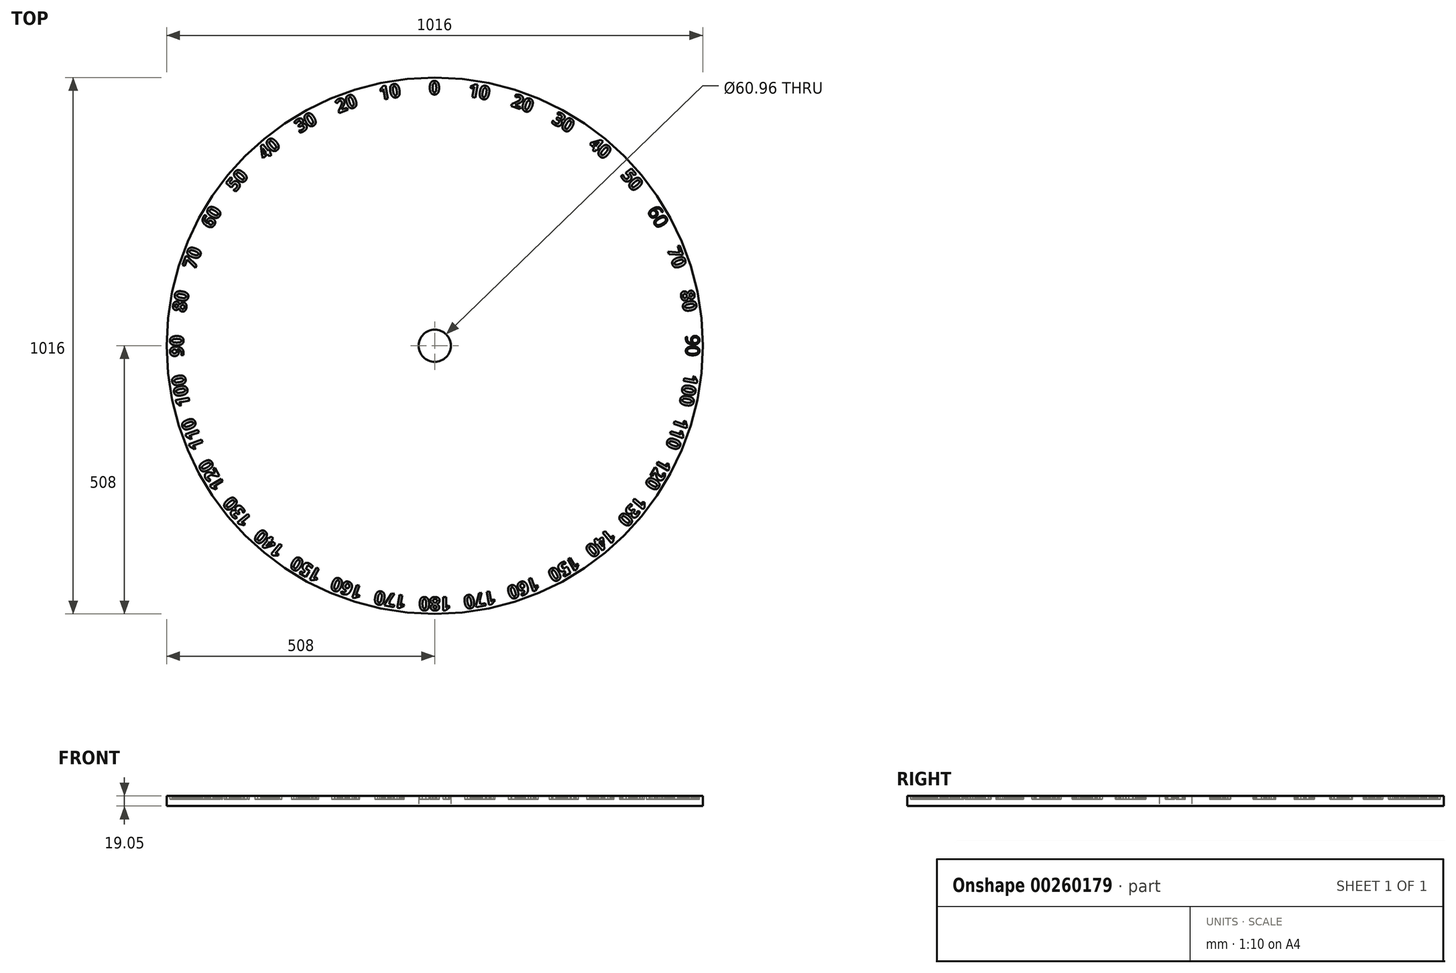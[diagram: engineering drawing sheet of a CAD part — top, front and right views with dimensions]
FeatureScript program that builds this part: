
annotation { "Feature Type Name" : "Feature", "Feature Type Description" : "" }
export const myFeature = defineFeature(function(context is Context, id is Id, definition is map)
    precondition{}
    {
        {
            var Q0;
            Q0=qCreatedBy(makeId("Top.planeOp"),FACE);
            var sketch = newSketch(context, id + "F0", { "sketchPlane" : qUnion([Q0])});
            skCircle(sketch, "E0", {"center": v(0, 0) * mm, "radius": 508 * mm});
            skCircle(sketch, "E1", {"center": v(0, 0) * mm, "radius": 30.48 * mm});
            skSolve(sketch);
        }
        {
            var Q0;
            Q0 = qSketchRegion(id + "F0", true);
            extrude(context, id + "F1", {"entities" : qUnion([Q0]), "depth" : 19.05 * mm});
        }
        {
            var Q0;
            Q0=makeQuery(id+"F1.opExtrude","CAP_FACE",FACE,{"disambiguationData":[OSD([sQuery(id+"F0.wireOp",EDGE,"E0"),sQuery(id+"F0.wireOp",EDGE,"E1")])],"isStart":false});
            var sketch = newSketch(context, id + "F2", { "sketchPlane" : qUnion([Q0])});
            skCircle(sketch, "E2", {"center": v(0, 0) * mm, "radius": 476.25 * mm, "construction": true});
            skLineSegment(sketch, "E3", {"start": v(0, 476.25) * mm, "end": v(0, 503.6) * mm});
            skLineSegment(sketch, "E4", {"start": v(0, 476.25) * mm, "end": v(50.8, 476.25) * mm});
            skText(sketch, "E5", { "text": "0", "fontName": "OpenSans-Bold.ttf"});
            skLineSegment(sketch, "E6.1.0", {"start": v(82.7, 469.01) * mm, "end": v(87.45, 495.95) * mm});
            skLineSegment(sketch, "E6.1.1", {"start": v(82.7, 469.01) * mm, "end": v(132.73, 460.2) * mm});
            skLineSegment(sketch, "E6.2.0", {"start": v(162.89, 447.53) * mm, "end": v(172.24, 473.23) * mm});
            skLineSegment(sketch, "E6.2.1", {"start": v(162.89, 447.53) * mm, "end": v(210.62, 430.15) * mm});
            skLineSegment(sketch, "E6.3.0", {"start": v(238.12, 412.44) * mm, "end": v(251.8, 436.13) * mm});
            skLineSegment(sketch, "E6.3.1", {"start": v(238.12, 412.44) * mm, "end": v(282.12, 387.04) * mm});
            skLineSegment(sketch, "E6.4.0", {"start": v(306.13, 364.83) * mm, "end": v(323.7, 385.78) * mm});
            skLineSegment(sketch, "E6.4.1", {"start": v(306.13, 364.83) * mm, "end": v(345.04, 332.18) * mm});
            skLineSegment(sketch, "E6.5.0", {"start": v(364.83, 306.13) * mm, "end": v(385.78, 323.7) * mm});
            skLineSegment(sketch, "E6.5.1", {"start": v(364.83, 306.13) * mm, "end": v(397.48, 267.21) * mm});
            skLineSegment(sketch, "E6.6.0", {"start": v(412.44, 238.13) * mm, "end": v(436.13, 251.8) * mm});
            skLineSegment(sketch, "E6.6.1", {"start": v(412.44, 238.13) * mm, "end": v(437.84, 194.13) * mm});
            skLineSegment(sketch, "E6.7.0", {"start": v(447.53, 162.89) * mm, "end": v(473.23, 172.24) * mm});
            skLineSegment(sketch, "E6.7.1", {"start": v(447.53, 162.89) * mm, "end": v(464.9, 115.15) * mm});
            skLineSegment(sketch, "E6.8.0", {"start": v(469.01, 82.7) * mm, "end": v(495.95, 87.45) * mm});
            skLineSegment(sketch, "E6.8.1", {"start": v(469.01, 82.7) * mm, "end": v(477.84, 32.67) * mm});
            skLineSegment(sketch, "E6.9.0", {"start": v(476.25, 0) * mm, "end": v(503.6, 0) * mm});
            skLineSegment(sketch, "E6.9.1", {"start": v(476.25, 0) * mm, "end": v(476.25, -50.8) * mm});
            skLineSegment(sketch, "E6.10.0", {"start": v(469.01, -82.7) * mm, "end": v(495.95, -87.45) * mm});
            skLineSegment(sketch, "E6.10.1", {"start": v(469.01, -82.7) * mm, "end": v(460.2, -132.73) * mm});
            skLineSegment(sketch, "E6.11.0", {"start": v(447.53, -162.89) * mm, "end": v(473.23, -172.24) * mm});
            skLineSegment(sketch, "E6.11.1", {"start": v(447.53, -162.89) * mm, "end": v(430.15, -210.62) * mm});
            skLineSegment(sketch, "E6.12.0", {"start": v(412.44, -238.12) * mm, "end": v(436.13, -251.8) * mm});
            skLineSegment(sketch, "E6.12.1", {"start": v(412.44, -238.12) * mm, "end": v(387.04, -282.12) * mm});
            skLineSegment(sketch, "E6.13.0", {"start": v(364.83, -306.13) * mm, "end": v(385.78, -323.7) * mm});
            skLineSegment(sketch, "E6.13.1", {"start": v(364.83, -306.13) * mm, "end": v(332.18, -345.04) * mm});
            skLineSegment(sketch, "E6.14.0", {"start": v(306.13, -364.83) * mm, "end": v(323.7, -385.78) * mm});
            skLineSegment(sketch, "E6.14.1", {"start": v(306.13, -364.83) * mm, "end": v(267.21, -397.48) * mm});
            skLineSegment(sketch, "E6.15.0", {"start": v(238.12, -412.44) * mm, "end": v(251.8, -436.13) * mm});
            skLineSegment(sketch, "E6.15.1", {"start": v(238.12, -412.44) * mm, "end": v(194.13, -437.84) * mm});
            skLineSegment(sketch, "E6.16.0", {"start": v(162.89, -447.53) * mm, "end": v(172.24, -473.23) * mm});
            skLineSegment(sketch, "E6.16.1", {"start": v(162.89, -447.53) * mm, "end": v(115.15, -464.9) * mm});
            skLineSegment(sketch, "E6.17.0", {"start": v(82.7, -469.01) * mm, "end": v(87.45, -495.95) * mm});
            skLineSegment(sketch, "E6.17.1", {"start": v(82.7, -469.01) * mm, "end": v(32.67, -477.84) * mm});
            skLineSegment(sketch, "E6.18.0", {"start": v(0, -476.25) * mm, "end": v(0, -503.6) * mm});
            skLineSegment(sketch, "E6.18.1", {"start": v(0, -476.25) * mm, "end": v(-50.8, -476.25) * mm});
            skLineSegment(sketch, "E6.19.0", {"start": v(-82.7, -469.01) * mm, "end": v(-87.45, -495.95) * mm});
            skLineSegment(sketch, "E6.19.1", {"start": v(-82.7, -469.01) * mm, "end": v(-132.73, -460.2) * mm});
            skLineSegment(sketch, "E6.20.0", {"start": v(-162.89, -447.53) * mm, "end": v(-172.24, -473.23) * mm});
            skLineSegment(sketch, "E6.20.1", {"start": v(-162.89, -447.53) * mm, "end": v(-210.62, -430.15) * mm});
            skLineSegment(sketch, "E6.21.0", {"start": v(-238.12, -412.44) * mm, "end": v(-251.8, -436.13) * mm});
            skLineSegment(sketch, "E6.21.1", {"start": v(-238.12, -412.44) * mm, "end": v(-282.12, -387.04) * mm});
            skLineSegment(sketch, "E6.22.0", {"start": v(-306.13, -364.83) * mm, "end": v(-323.7, -385.78) * mm});
            skLineSegment(sketch, "E6.22.1", {"start": v(-306.13, -364.83) * mm, "end": v(-345.04, -332.18) * mm});
            skLineSegment(sketch, "E6.23.0", {"start": v(-364.83, -306.13) * mm, "end": v(-385.78, -323.7) * mm});
            skLineSegment(sketch, "E6.23.1", {"start": v(-364.83, -306.13) * mm, "end": v(-397.48, -267.21) * mm});
            skLineSegment(sketch, "E6.24.0", {"start": v(-412.44, -238.13) * mm, "end": v(-436.13, -251.8) * mm});
            skLineSegment(sketch, "E6.24.1", {"start": v(-412.44, -238.13) * mm, "end": v(-437.84, -194.13) * mm});
            skLineSegment(sketch, "E6.25.0", {"start": v(-447.53, -162.89) * mm, "end": v(-473.23, -172.24) * mm});
            skLineSegment(sketch, "E6.25.1", {"start": v(-447.53, -162.89) * mm, "end": v(-464.9, -115.15) * mm});
            skLineSegment(sketch, "E6.26.0", {"start": v(-469.01, -82.7) * mm, "end": v(-495.95, -87.45) * mm});
            skLineSegment(sketch, "E6.26.1", {"start": v(-469.01, -82.7) * mm, "end": v(-477.84, -32.67) * mm});
            skLineSegment(sketch, "E6.27.0", {"start": v(-476.25, 0) * mm, "end": v(-503.6, 0) * mm});
            skLineSegment(sketch, "E6.27.1", {"start": v(-476.25, 0) * mm, "end": v(-476.25, 50.8) * mm});
            skLineSegment(sketch, "E6.28.0", {"start": v(-469.01, 82.7) * mm, "end": v(-495.95, 87.45) * mm});
            skLineSegment(sketch, "E6.28.1", {"start": v(-469.01, 82.7) * mm, "end": v(-460.2, 132.73) * mm});
            skLineSegment(sketch, "E6.29.0", {"start": v(-447.53, 162.89) * mm, "end": v(-473.23, 172.24) * mm});
            skLineSegment(sketch, "E6.29.1", {"start": v(-447.53, 162.89) * mm, "end": v(-430.15, 210.62) * mm});
            skLineSegment(sketch, "E6.30.0", {"start": v(-412.44, 238.13) * mm, "end": v(-436.13, 251.8) * mm});
            skLineSegment(sketch, "E6.30.1", {"start": v(-412.44, 238.13) * mm, "end": v(-387.04, 282.12) * mm});
            skLineSegment(sketch, "E6.31.0", {"start": v(-364.83, 306.13) * mm, "end": v(-385.78, 323.7) * mm});
            skLineSegment(sketch, "E6.31.1", {"start": v(-364.83, 306.13) * mm, "end": v(-332.18, 345.04) * mm});
            skLineSegment(sketch, "E6.32.0", {"start": v(-306.13, 364.83) * mm, "end": v(-323.7, 385.78) * mm});
            skLineSegment(sketch, "E6.32.1", {"start": v(-306.13, 364.83) * mm, "end": v(-267.21, 397.48) * mm});
            skLineSegment(sketch, "E6.33.0", {"start": v(-238.12, 412.44) * mm, "end": v(-251.8, 436.13) * mm});
            skLineSegment(sketch, "E6.33.1", {"start": v(-238.12, 412.44) * mm, "end": v(-194.13, 437.84) * mm});
            skLineSegment(sketch, "E6.34.0", {"start": v(-162.89, 447.53) * mm, "end": v(-172.24, 473.23) * mm});
            skLineSegment(sketch, "E6.34.1", {"start": v(-162.89, 447.53) * mm, "end": v(-115.15, 464.9) * mm});
            skLineSegment(sketch, "E6.35.0", {"start": v(-82.7, 469.01) * mm, "end": v(-87.45, 495.95) * mm});
            skLineSegment(sketch, "E6.35.1", {"start": v(-82.7, 469.01) * mm, "end": v(-32.67, 477.84) * mm});
            skLineSegment(sketch, "E6.anchor1", {"start": v(0, 0) * mm, "end": v(0, 476.25) * mm, "construction": true});
            skLineSegment(sketch, "E6.anchor2", {"start": v(0, 0) * mm, "end": v(-82.7, 469.01) * mm, "construction": true});
            skText(sketch, "E7", { "text": "10", "fontName": "OpenSans-Bold.ttf"});
            skText(sketch, "E8", { "text": "20", "fontName": "OpenSans-Bold.ttf"});
            skText(sketch, "E9", { "text": "30", "fontName": "OpenSans-Bold.ttf"});
            skText(sketch, "E10", { "text": "40", "fontName": "OpenSans-Bold.ttf"});
            skText(sketch, "E11", { "text": "50", "fontName": "OpenSans-Bold.ttf"});
            skText(sketch, "E12", { "text": "60", "fontName": "OpenSans-Regular.ttf"});
            skText(sketch, "E13", { "text": "70", "fontName": "OpenSans-Bold.ttf"});
            skText(sketch, "E14", { "text": "80", "fontName": "OpenSans-Bold.ttf"});
            skText(sketch, "E15", { "text": "90\n", "fontName": "OpenSans-Regular.ttf"});
            skText(sketch, "E16", { "text": "100", "fontName": "OpenSans-Bold.ttf"});
            skText(sketch, "E17", { "text": "110", "fontName": "OpenSans-Bold.ttf"});
            skText(sketch, "E18", { "text": "120", "fontName": "OpenSans-Bold.ttf"});
            skText(sketch, "E19", { "text": "130", "fontName": "OpenSans-Bold.ttf"});
            skText(sketch, "E20", { "text": "140", "fontName": "OpenSans-Bold.ttf"});
            skText(sketch, "E21", { "text": "150", "fontName": "OpenSans-Bold.ttf"});
            skText(sketch, "E22", { "text": "160", "fontName": "OpenSans-Bold.ttf"});
            skText(sketch, "E23", { "text": "170", "fontName": "OpenSans-Bold.ttf"});
            skPoint(sketch, "E24.endSnap0", {"position": v(0, 238.12) * mm});
            skText(sketch, "E25", { "text": "10", "fontName": "OpenSans-Bold.ttf"});
            skText(sketch, "E26", { "text": "20", "fontName": "OpenSans-Bold.ttf"});
            skText(sketch, "E27", { "text": "30", "fontName": "OpenSans-Bold.ttf"});
            skText(sketch, "E28", { "text": "40", "fontName": "OpenSans-Bold.ttf"});
            skText(sketch, "E29", { "text": "50", "fontName": "OpenSans-Bold.ttf"});
            skText(sketch, "E30", { "text": "60", "fontName": "OpenSans-Bold.ttf"});
            skText(sketch, "E31", { "text": "70", "fontName": "OpenSans-Bold.ttf"});
            skText(sketch, "E32", { "text": "80", "fontName": "OpenSans-Bold.ttf"});
            skText(sketch, "E33", { "text": "90", "fontName": "OpenSans-Bold.ttf"});
            skText(sketch, "E34", { "text": "100", "fontName": "OpenSans-Bold.ttf"});
            skText(sketch, "E35", { "text": "110", "fontName": "OpenSans-Bold.ttf"});
            skText(sketch, "E36", { "text": "120", "fontName": "OpenSans-Bold.ttf"});
            skText(sketch, "E37", { "text": "130", "fontName": "OpenSans-Bold.ttf"});
            skText(sketch, "E38", { "text": "140", "fontName": "OpenSans-Bold.ttf"});
            skText(sketch, "E39", { "text": "150", "fontName": "OpenSans-Bold.ttf"});
            skText(sketch, "E40", { "text": "160", "fontName": "OpenSans-Bold.ttf"});
            skText(sketch, "E41", { "text": "170", "fontName": "OpenSans-Bold.ttf"});
            skPoint(sketch, "E41.firstSnap0", {"position": v(-5.2, -310.82) * mm});
            skText(sketch, "E42", { "text": "180", "fontName": "OpenSans-Bold.ttf"});
            const initialGuessF2  = {"E5": [-0.01058, 0.47625, 1, 0, 0.0254], "E7": [0.06236, 0.4726, 0.9848, -0.17365, 0.0254], "E8": [0.14348, 0.4546, 0.9397, -0.34202, 0.0254], "E9": [0.22024, 0.42277, 0.86603, -0.5, 0.0254], "E10": [0.2903, 0.3781, 0.76604, -0.64279, 0.0254], "E11": [0.35155, 0.32195, 0.64279, -0.76604, 0.0254], "E12": [0.40223, 0.25582, 0.5, -0.86603, 0.0254], "E13": [0.44047, 0.1823, 0.34202, -0.9397, 0.0254], "E14": [0.46543, 0.10304, 0.17365, -0.9848, 0.0254], "E15": [0.47625, 0.02044, 0, -1, 0.0254], "E16": [0.47435, -0.05245, -0.17365, -0.9848, 0.0254], "E17": [0.45804, -0.13402, -0.34202, -0.9397, 0.0254], "E18": [0.4278, -0.21152, -0.5, -0.86603, 0.0254], "E19": [0.38457, -0.2826, -0.64279, -0.76604, 0.0254], "E20": [0.32966, -0.34508, -0.76604, -0.64279, 0.0254], "E21": [0.26473, -0.39708, -0.86603, -0.5, 0.0254], "E22": [0.19175, -0.43702, -0.9397, -0.34202, 0.0254], "E23": [0.11295, -0.46368, -0.9848, -0.17365, 0.0254], "E25": [-0.10304, 0.46543, 0.9848, 0.17365, 0.0254], "E26": [-0.1823, 0.44047, 0.9397, 0.34202, 0.0254], "E27": [-0.256, 0.40212, 0.86603, 0.5, 0.0254], "E28": [-0.32195, 0.35155, 0.76604, 0.64279, 0.0254], "E29": [-0.3781, 0.2903, 0.64279, 0.76604, 0.0254], "E30": [-0.42277, 0.22024, 0.5, 0.86603, 0.0254], "E31": [-0.4546, 0.14348, 0.34202, 0.9397, 0.0254], "E32": [-0.4726, 0.06236, 0.17365, 0.9848, 0.0254], "E33": [-0.47625, -0.02065, 0, 1, 0.0254], "E34": [-0.46368, -0.11295, -0.17365, 0.9848, 0.0254], "E35": [-0.43702, -0.19175, -0.34202, 0.9397, 0.0254], "E36": [-0.39708, -0.26473, -0.5, 0.86603, 0.0254], "E37": [-0.34508, -0.32966, -0.64279, 0.76604, 0.0254], "E38": [-0.2826, -0.38457, -0.76604, 0.64279, 0.0254], "E39": [-0.21152, -0.4278, -0.86603, 0.5, 0.0254], "E40": [-0.13402, -0.45804, -0.9397, 0.34202, 0.0254], "E41": [-0.05245, -0.47435, -0.9848, 0.17365, 0.0254], "E42": [0.03072, -0.47625, -1, 0, 0.0254]};
            skSetInitialGuess(sketch, initialGuessF2);
            skSolve(sketch);
        }
        {
            var Q0;
            Q0 = qSketchRegion(id + "F2", true);
            extrude(context, id + "F3", {"entities" : qUnion([Q0]), "operationType" : NewBodyOperationType.REMOVE, "oppositeDirection" : true, "depth" : 6.35 * mm});
        }
    });
